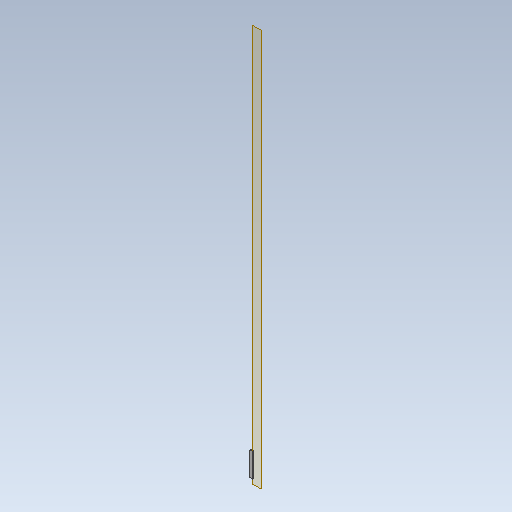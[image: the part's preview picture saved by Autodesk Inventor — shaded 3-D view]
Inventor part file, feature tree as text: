
AUTODESK INVENTOR PART (.ipt)
format: ipt  version: 2020.1 (Build 241239000, 239)  size: 95,232 bytes
history: native  units: mm
features: other x3, plane x1, extrude x1, sketch x1
ambient origin geometry x8: Origin, YZ Plane, XZ Plane, XY Plane, X Axis, Y Axis, Z Axis, Center Point
bodies: Solid1 (feature_tree)
feature tree (6):
  plane  "Work Plane1"
  extrude  "Extrusion1"  Depth=80.0mm
  sketch  "Sketch1"  dims[d0=10.0mm d1=80.0mm d2=4.0mm d3=0.0mm]
  parser-record x1  (decoder bookkeeping rows leaked as tree rows — omitted from the tree; the rows remain in map.json)
  other  "håndfang.iam"
  other  "stang:2"
note: 1 file-system path scrubbed to <path> (originals preserved in map.json)
